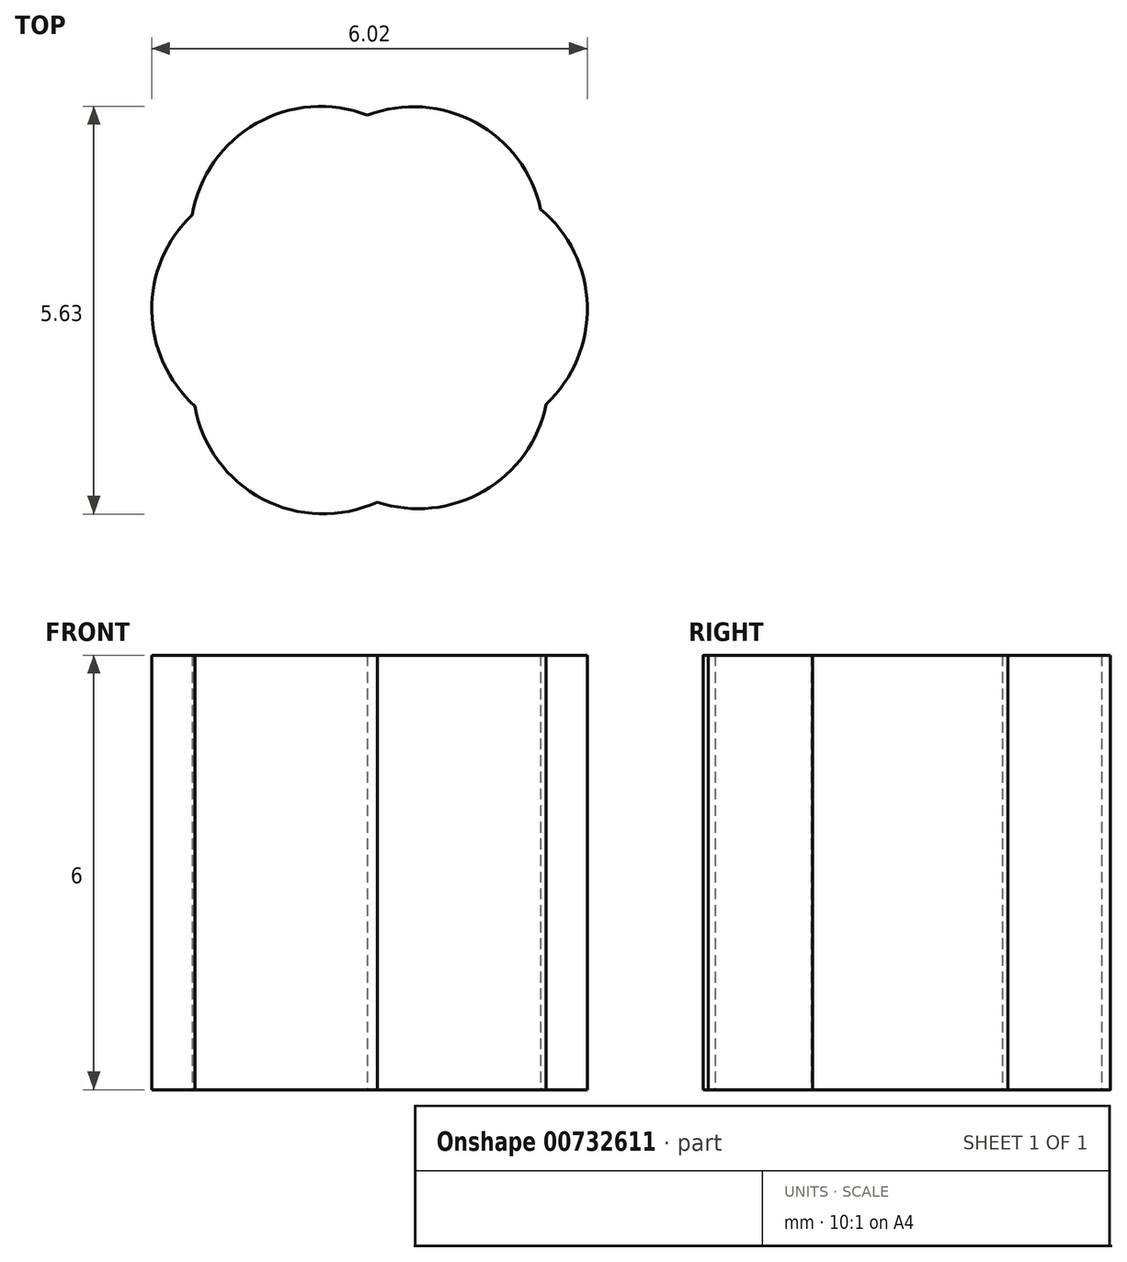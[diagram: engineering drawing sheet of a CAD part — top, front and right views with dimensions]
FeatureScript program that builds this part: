
annotation { "Feature Type Name" : "Feature", "Feature Type Description" : "" }
export const myFeature = defineFeature(function(context is Context, id is Id, definition is map)
    precondition{}
    {
        {
            var Q0;
            Q0=qCreatedBy(makeId("Top.planeOp"),FACE);
            var sketch = newSketch(context, id + "F0", { "sketchPlane" : qUnion([Q0])});
            skCircle(sketch, "E0", {"center": v(0.62, 1) * mm, "radius": 1.8 * mm});
            skCircle(sketch, "E1", {"center": v(1.22, 0) * mm, "radius": 1.8 * mm});
            skCircle(sketch, "E2", {"center": v(-0.66, 1) * mm, "radius": 1.8 * mm});
            skCircle(sketch, "E3", {"center": v(0.69, -0.96) * mm, "radius": 1.8 * mm});
            skCircle(sketch, "E4", {"center": v(-0.63, -1.03) * mm, "radius": 1.8 * mm});
            skCircle(sketch, "E5", {"center": v(-1.2, 0) * mm, "radius": 1.8 * mm});
            skSolve(sketch);
        }
        {
            var Q0;
            {var subQ0=sQuery(id+"F0.wireOp",EDGE,"E5");var subQ1=sQuery(id+"F0.wireOp",EDGE,"E0");var subQ2=makeQuery(id+"F0.imprint","INTERSECT",VERTEX,{"disambiguationData":[OD(0.0)],"derivedFrom":[subQ1,subQ0]});Q0=makeQuery(id+"F0.imprint","IMPRINT",FACE,{"disambiguationData":[TD([[makeQuery(id+"F0.imprint","IMPRINT",EDGE,{"disambiguationData":[TD([[subQ2,-1.0]])],"derivedFrom":subQ1}),-1.0]])]});}
            var Q1;
            {var subQ0=sQuery(id+"F0.wireOp",EDGE,"E2");var subQ1=sQuery(id+"F0.wireOp",EDGE,"E0");var subQ2=makeQuery(id+"F0.imprint","INTERSECT",VERTEX,{"disambiguationData":[OD(0.0)],"derivedFrom":[subQ1,subQ0]});Q1=makeQuery(id+"F0.imprint","IMPRINT",FACE,{"disambiguationData":[TD([[makeQuery(id+"F0.imprint","IMPRINT",EDGE,{"disambiguationData":[TD([[subQ2,-1.0]])],"derivedFrom":subQ1}),-1.0]])]});}
            var Q2;
            {var subQ0=sQuery(id+"F0.wireOp",EDGE,"E2");var subQ1=sQuery(id+"F0.wireOp",EDGE,"E0");var subQ2=makeQuery(id+"F0.imprint","INTERSECT",VERTEX,{"disambiguationData":[OD(0.0)],"derivedFrom":[subQ1,subQ0]});Q2=makeQuery(id+"F0.imprint","IMPRINT",FACE,{"disambiguationData":[TD([[makeQuery(id+"F0.imprint","IMPRINT",EDGE,{"disambiguationData":[TD([[subQ2,-1.0]])],"derivedFrom":subQ1}),1.0]])]});}
            var Q3;
            {var subQ0=sQuery(id+"F0.wireOp",EDGE,"E2");var subQ1=sQuery(id+"F0.wireOp",EDGE,"E0");var subQ2=makeQuery(id+"F0.imprint","INTERSECT",VERTEX,{"disambiguationData":[OD(0.0)],"derivedFrom":[subQ1,subQ0]});Q3=makeQuery(id+"F0.imprint","IMPRINT",FACE,{"disambiguationData":[TD([[makeQuery(id+"F0.imprint","IMPRINT",EDGE,{"disambiguationData":[TD([[subQ2,1.0]])],"derivedFrom":subQ1}),1.0]])]});}
            var Q4;
            {var subQ0=sQuery(id+"F0.wireOp",EDGE,"E1");var subQ1=sQuery(id+"F0.wireOp",EDGE,"E0");var subQ2=makeQuery(id+"F0.imprint","INTERSECT",VERTEX,{"disambiguationData":[OD(0.0)],"derivedFrom":[subQ1,subQ0]});Q4=makeQuery(id+"F0.imprint","IMPRINT",FACE,{"disambiguationData":[TD([[makeQuery(id+"F0.imprint","IMPRINT",EDGE,{"disambiguationData":[TD([[subQ2,1.0]])],"derivedFrom":subQ1}),1.0]])]});}
            var Q5;
            {var subQ0=sQuery(id+"F0.wireOp",EDGE,"E5");var subQ1=sQuery(id+"F0.wireOp",EDGE,"E2");var subQ2=makeQuery(id+"F0.imprint","INTERSECT",VERTEX,{"disambiguationData":[OD(0.0)],"derivedFrom":[subQ1,subQ0]});Q5=makeQuery(id+"F0.imprint","IMPRINT",FACE,{"disambiguationData":[TD([[makeQuery(id+"F0.imprint","IMPRINT",EDGE,{"disambiguationData":[TD([[subQ2,-1.0]])],"derivedFrom":subQ1}),-1.0]])]});}
            var Q6;
            {var subQ0=sQuery(id+"F0.wireOp",EDGE,"E4");var subQ1=sQuery(id+"F0.wireOp",EDGE,"E2");var subQ2=makeQuery(id+"F0.imprint","INTERSECT",VERTEX,{"disambiguationData":[OD(0.0)],"derivedFrom":[subQ1,subQ0]});Q6=makeQuery(id+"F0.imprint","IMPRINT",FACE,{"disambiguationData":[TD([[makeQuery(id+"F0.imprint","IMPRINT",EDGE,{"disambiguationData":[TD([[subQ2,-1.0]])],"derivedFrom":subQ1}),-1.0]])]});}
            var Q7;
            {var subQ0=sQuery(id+"F0.wireOp",EDGE,"E4");var subQ1=sQuery(id+"F0.wireOp",EDGE,"E0");var subQ2=makeQuery(id+"F0.imprint","INTERSECT",VERTEX,{"disambiguationData":[OD(0.0)],"derivedFrom":[subQ1,subQ0]});Q7=makeQuery(id+"F0.imprint","IMPRINT",FACE,{"disambiguationData":[TD([[makeQuery(id+"F0.imprint","IMPRINT",EDGE,{"disambiguationData":[TD([[subQ2,-1.0]])],"derivedFrom":subQ1}),-1.0]])]});}
            var Q8;
            {var subQ0=sQuery(id+"F0.wireOp",EDGE,"E4");var subQ1=sQuery(id+"F0.wireOp",EDGE,"E0");var subQ2=makeQuery(id+"F0.imprint","INTERSECT",VERTEX,{"disambiguationData":[OD(0.0)],"derivedFrom":[subQ1,subQ0]});Q8=makeQuery(id+"F0.imprint","IMPRINT",FACE,{"disambiguationData":[TD([[makeQuery(id+"F0.imprint","IMPRINT",EDGE,{"disambiguationData":[TD([[subQ2,-1.0]])],"derivedFrom":subQ1}),1.0]])]});}
            var Q9;
            {var subQ0=sQuery(id+"F0.wireOp",EDGE,"E5");var subQ1=sQuery(id+"F0.wireOp",EDGE,"E0");var subQ2=makeQuery(id+"F0.imprint","INTERSECT",VERTEX,{"disambiguationData":[OD(0.0)],"derivedFrom":[subQ1,subQ0]});Q9=makeQuery(id+"F0.imprint","IMPRINT",FACE,{"disambiguationData":[TD([[makeQuery(id+"F0.imprint","IMPRINT",EDGE,{"disambiguationData":[TD([[subQ2,-1.0]])],"derivedFrom":subQ1}),1.0]])]});}
            var Q10;
            {var subQ0=sQuery(id+"F0.wireOp",EDGE,"E5");var subQ1=sQuery(id+"F0.wireOp",EDGE,"E1");var subQ2=makeQuery(id+"F0.imprint","INTERSECT",VERTEX,{"disambiguationData":[OD(0.0)],"derivedFrom":[subQ1,subQ0]});Q10=makeQuery(id+"F0.imprint","IMPRINT",FACE,{"disambiguationData":[TD([[makeQuery(id+"F0.imprint","IMPRINT",EDGE,{"disambiguationData":[TD([[subQ2,-1.0]])],"derivedFrom":subQ1}),1.0]])]});}
            var Q11;
            {var subQ0=sQuery(id+"F0.wireOp",EDGE,"E4");var subQ1=sQuery(id+"F0.wireOp",EDGE,"E1");var subQ2=makeQuery(id+"F0.imprint","INTERSECT",VERTEX,{"disambiguationData":[OD(0.0)],"derivedFrom":[subQ1,subQ0]});Q11=makeQuery(id+"F0.imprint","IMPRINT",FACE,{"disambiguationData":[TD([[makeQuery(id+"F0.imprint","IMPRINT",EDGE,{"disambiguationData":[TD([[subQ2,-1.0]])],"derivedFrom":subQ1}),1.0]])]});}
            var Q12;
            {var subQ1=sQuery(id+"F0.wireOp",EDGE,"E1");var subQ6=sQuery(id+"F0.wireOp",EDGE,"E0");var subQ11=makeQuery(id+"F0.imprint","INTERSECT",VERTEX,{"disambiguationData":[OD(1.0)],"derivedFrom":[subQ6,subQ1]});Q12=makeQuery(id+"F0.imprint","IMPRINT",FACE,{"disambiguationData":[TD([[makeQuery(id+"F0.imprint","IMPRINT",EDGE,{"disambiguationData":[TD([[subQ11,-1.0]])],"derivedFrom":subQ6}),1.0]])]});}
            var Q13;
            {var subQ0=sQuery(id+"F0.wireOp",EDGE,"E5");var subQ1=sQuery(id+"F0.wireOp",EDGE,"E3");var subQ2=makeQuery(id+"F0.imprint","INTERSECT",VERTEX,{"disambiguationData":[OD(0.0)],"derivedFrom":[subQ1,subQ0]});Q13=makeQuery(id+"F0.imprint","IMPRINT",FACE,{"disambiguationData":[TD([[makeQuery(id+"F0.imprint","IMPRINT",EDGE,{"disambiguationData":[TD([[subQ2,-1.0]])],"derivedFrom":subQ1}),1.0]])]});}
            var Q14;
            {var subQ0=sQuery(id+"F0.wireOp",EDGE,"E4");var subQ1=sQuery(id+"F0.wireOp",EDGE,"E2");var subQ2=makeQuery(id+"F0.imprint","INTERSECT",VERTEX,{"disambiguationData":[OD(1.0)],"derivedFrom":[subQ1,subQ0]});Q14=makeQuery(id+"F0.imprint","IMPRINT",FACE,{"disambiguationData":[TD([[makeQuery(id+"F0.imprint","IMPRINT",EDGE,{"disambiguationData":[TD([[subQ2,-1.0]])],"derivedFrom":subQ1}),1.0]])]});}
            var Q15;
            {var subQ0=sQuery(id+"F0.wireOp",EDGE,"E5");var subQ1=sQuery(id+"F0.wireOp",EDGE,"E2");var subQ2=makeQuery(id+"F0.imprint","INTERSECT",VERTEX,{"disambiguationData":[OD(1.0)],"derivedFrom":[subQ1,subQ0]});Q15=makeQuery(id+"F0.imprint","IMPRINT",FACE,{"disambiguationData":[TD([[makeQuery(id+"F0.imprint","IMPRINT",EDGE,{"disambiguationData":[TD([[subQ2,-1.0]])],"derivedFrom":subQ1}),1.0]])]});}
            var Q16;
            {var subQ0=sQuery(id+"F0.wireOp",EDGE,"E4");var subQ1=sQuery(id+"F0.wireOp",EDGE,"E0");var subQ2=makeQuery(id+"F0.imprint","INTERSECT",VERTEX,{"disambiguationData":[OD(1.0)],"derivedFrom":[subQ1,subQ0]});Q16=makeQuery(id+"F0.imprint","IMPRINT",FACE,{"disambiguationData":[TD([[makeQuery(id+"F0.imprint","IMPRINT",EDGE,{"disambiguationData":[TD([[subQ2,-1.0]])],"derivedFrom":subQ1}),1.0]])]});}
            var Q17;
            {var subQ0=sQuery(id+"F0.wireOp",EDGE,"E2");var subQ1=sQuery(id+"F0.wireOp",EDGE,"E0");var subQ2=makeQuery(id+"F0.imprint","INTERSECT",VERTEX,{"disambiguationData":[OD(1.0)],"derivedFrom":[subQ1,subQ0]});Q17=makeQuery(id+"F0.imprint","IMPRINT",FACE,{"disambiguationData":[TD([[makeQuery(id+"F0.imprint","IMPRINT",EDGE,{"disambiguationData":[TD([[subQ2,-1.0]])],"derivedFrom":subQ1}),1.0]])]});}
            var Q18;
            {var subQ0=sQuery(id+"F0.wireOp",EDGE,"E3");var subQ1=sQuery(id+"F0.wireOp",EDGE,"E0");var subQ2=makeQuery(id+"F0.imprint","INTERSECT",VERTEX,{"disambiguationData":[OD(0.0)],"derivedFrom":[subQ1,subQ0]});Q18=makeQuery(id+"F0.imprint","IMPRINT",FACE,{"disambiguationData":[TD([[makeQuery(id+"F0.imprint","IMPRINT",EDGE,{"disambiguationData":[TD([[subQ2,-1.0]])],"derivedFrom":subQ1}),1.0]])]});}
            var Q19;
            {var subQ0=sQuery(id+"F0.wireOp",EDGE,"E3");var subQ1=sQuery(id+"F0.wireOp",EDGE,"E0");var subQ2=makeQuery(id+"F0.imprint","INTERSECT",VERTEX,{"disambiguationData":[OD(0.0)],"derivedFrom":[subQ1,subQ0]});Q19=makeQuery(id+"F0.imprint","IMPRINT",FACE,{"disambiguationData":[TD([[makeQuery(id+"F0.imprint","IMPRINT",EDGE,{"disambiguationData":[TD([[subQ2,-1.0]])],"derivedFrom":subQ1}),-1.0]])]});}
            var Q20;
            {var subQ0=sQuery(id+"F0.wireOp",EDGE,"E1");var subQ1=sQuery(id+"F0.wireOp",EDGE,"E0");var subQ2=makeQuery(id+"F0.imprint","INTERSECT",VERTEX,{"disambiguationData":[OD(1.0)],"derivedFrom":[subQ1,subQ0]});Q20=makeQuery(id+"F0.imprint","IMPRINT",FACE,{"disambiguationData":[TD([[makeQuery(id+"F0.imprint","IMPRINT",EDGE,{"disambiguationData":[TD([[subQ2,-1.0]])],"derivedFrom":subQ1}),-1.0]])]});}
            var Q21;
            {var subQ0=sQuery(id+"F0.wireOp",EDGE,"E2");var subQ1=sQuery(id+"F0.wireOp",EDGE,"E1");var subQ2=makeQuery(id+"F0.imprint","INTERSECT",VERTEX,{"disambiguationData":[OD(1.0)],"derivedFrom":[subQ1,subQ0]});Q21=makeQuery(id+"F0.imprint","IMPRINT",FACE,{"disambiguationData":[TD([[makeQuery(id+"F0.imprint","IMPRINT",EDGE,{"disambiguationData":[TD([[subQ2,-1.0]])],"derivedFrom":subQ1}),-1.0]])]});}
            var Q22;
            {var subQ0=sQuery(id+"F0.wireOp",EDGE,"E2");var subQ1=sQuery(id+"F0.wireOp",EDGE,"E0");var subQ2=makeQuery(id+"F0.imprint","INTERSECT",VERTEX,{"disambiguationData":[OD(1.0)],"derivedFrom":[subQ1,subQ0]});Q22=makeQuery(id+"F0.imprint","IMPRINT",FACE,{"disambiguationData":[TD([[makeQuery(id+"F0.imprint","IMPRINT",EDGE,{"disambiguationData":[TD([[subQ2,-1.0]])],"derivedFrom":subQ1}),-1.0]])]});}
            var Q23;
            {var subQ0=sQuery(id+"F0.wireOp",EDGE,"E4");var subQ1=sQuery(id+"F0.wireOp",EDGE,"E0");var subQ2=makeQuery(id+"F0.imprint","INTERSECT",VERTEX,{"disambiguationData":[OD(1.0)],"derivedFrom":[subQ1,subQ0]});Q23=makeQuery(id+"F0.imprint","IMPRINT",FACE,{"disambiguationData":[TD([[makeQuery(id+"F0.imprint","IMPRINT",EDGE,{"disambiguationData":[TD([[subQ2,-1.0]])],"derivedFrom":subQ1}),-1.0]])]});}
            var Q24;
            {var subQ0=sQuery(id+"F0.wireOp",EDGE,"E1");var subQ1=sQuery(id+"F0.wireOp",EDGE,"E0");var subQ2=makeQuery(id+"F0.imprint","INTERSECT",VERTEX,{"disambiguationData":[OD(0.0)],"derivedFrom":[subQ1,subQ0]});Q24=makeQuery(id+"F0.imprint","IMPRINT",FACE,{"disambiguationData":[TD([[makeQuery(id+"F0.imprint","IMPRINT",EDGE,{"disambiguationData":[TD([[subQ2,1.0]])],"derivedFrom":subQ1}),-1.0]])]});}
            var Q25;
            {var subQ0=sQuery(id+"F0.wireOp",EDGE,"E4");var subQ1=sQuery(id+"F0.wireOp",EDGE,"E3");var subQ2=makeQuery(id+"F0.imprint","INTERSECT",VERTEX,{"disambiguationData":[OD(0.0)],"derivedFrom":[subQ1,subQ0]});Q25=makeQuery(id+"F0.imprint","IMPRINT",FACE,{"disambiguationData":[TD([[makeQuery(id+"F0.imprint","IMPRINT",EDGE,{"disambiguationData":[TD([[subQ2,1.0]])],"derivedFrom":subQ1}),-1.0]])]});}
            var Q26;
            {var subQ0=sQuery(id+"F0.wireOp",EDGE,"E5");var subQ1=sQuery(id+"F0.wireOp",EDGE,"E0");var subQ2=makeQuery(id+"F0.imprint","INTERSECT",VERTEX,{"disambiguationData":[OD(1.0)],"derivedFrom":[subQ1,subQ0]});Q26=makeQuery(id+"F0.imprint","IMPRINT",FACE,{"disambiguationData":[TD([[makeQuery(id+"F0.imprint","IMPRINT",EDGE,{"disambiguationData":[TD([[subQ2,-1.0]])],"derivedFrom":subQ1}),-1.0]])]});}
            var Q27;
            {var subQ0=sQuery(id+"F0.wireOp",EDGE,"E5");var subQ1=sQuery(id+"F0.wireOp",EDGE,"E1");var subQ2=makeQuery(id+"F0.imprint","INTERSECT",VERTEX,{"disambiguationData":[OD(1.0)],"derivedFrom":[subQ1,subQ0]});Q27=makeQuery(id+"F0.imprint","IMPRINT",FACE,{"disambiguationData":[TD([[makeQuery(id+"F0.imprint","IMPRINT",EDGE,{"disambiguationData":[TD([[subQ2,-1.0]])],"derivedFrom":subQ1}),-1.0]])]});}
            var Q28;
            {var subQ0=sQuery(id+"F0.wireOp",EDGE,"E3");var subQ1=sQuery(id+"F0.wireOp",EDGE,"E1");var subQ2=makeQuery(id+"F0.imprint","INTERSECT",VERTEX,{"disambiguationData":[OD(0.0)],"derivedFrom":[subQ1,subQ0]});Q28=makeQuery(id+"F0.imprint","IMPRINT",FACE,{"disambiguationData":[TD([[makeQuery(id+"F0.imprint","IMPRINT",EDGE,{"disambiguationData":[TD([[subQ2,1.0]])],"derivedFrom":subQ1}),-1.0]])]});}
            var Q29;
            {var subQ0=sQuery(id+"F0.wireOp",EDGE,"E2");var subQ1=sQuery(id+"F0.wireOp",EDGE,"E1");var subQ2=makeQuery(id+"F0.imprint","INTERSECT",VERTEX,{"disambiguationData":[OD(0.0)],"derivedFrom":[subQ1,subQ0]});Q29=makeQuery(id+"F0.imprint","IMPRINT",FACE,{"disambiguationData":[TD([[makeQuery(id+"F0.imprint","IMPRINT",EDGE,{"disambiguationData":[TD([[subQ2,-1.0]])],"derivedFrom":subQ1}),1.0]])]});}
            var Q30;
            {var subQ0=sQuery(id+"F0.wireOp",EDGE,"E5");var subQ1=sQuery(id+"F0.wireOp",EDGE,"E0");var subQ2=makeQuery(id+"F0.imprint","INTERSECT",VERTEX,{"disambiguationData":[OD(1.0)],"derivedFrom":[subQ1,subQ0]});Q30=makeQuery(id+"F0.imprint","IMPRINT",FACE,{"disambiguationData":[TD([[makeQuery(id+"F0.imprint","IMPRINT",EDGE,{"disambiguationData":[TD([[subQ2,-1.0]])],"derivedFrom":subQ1}),1.0]])]});}
            extrude(context, id + "F1", {"entities" : qUnion([Q0, Q1, Q2, Q3, Q4, Q5, Q6, Q7, Q8, Q9, Q10, Q11, Q12, Q13, Q14, Q15, Q16, Q17, Q18, Q19, Q20, Q21, Q22, Q23, Q24, Q25, Q26, Q27, Q28, Q29, Q30]), "depth" : 6 * mm, "offsetDistance" : 25 * mm});
        }
    });
